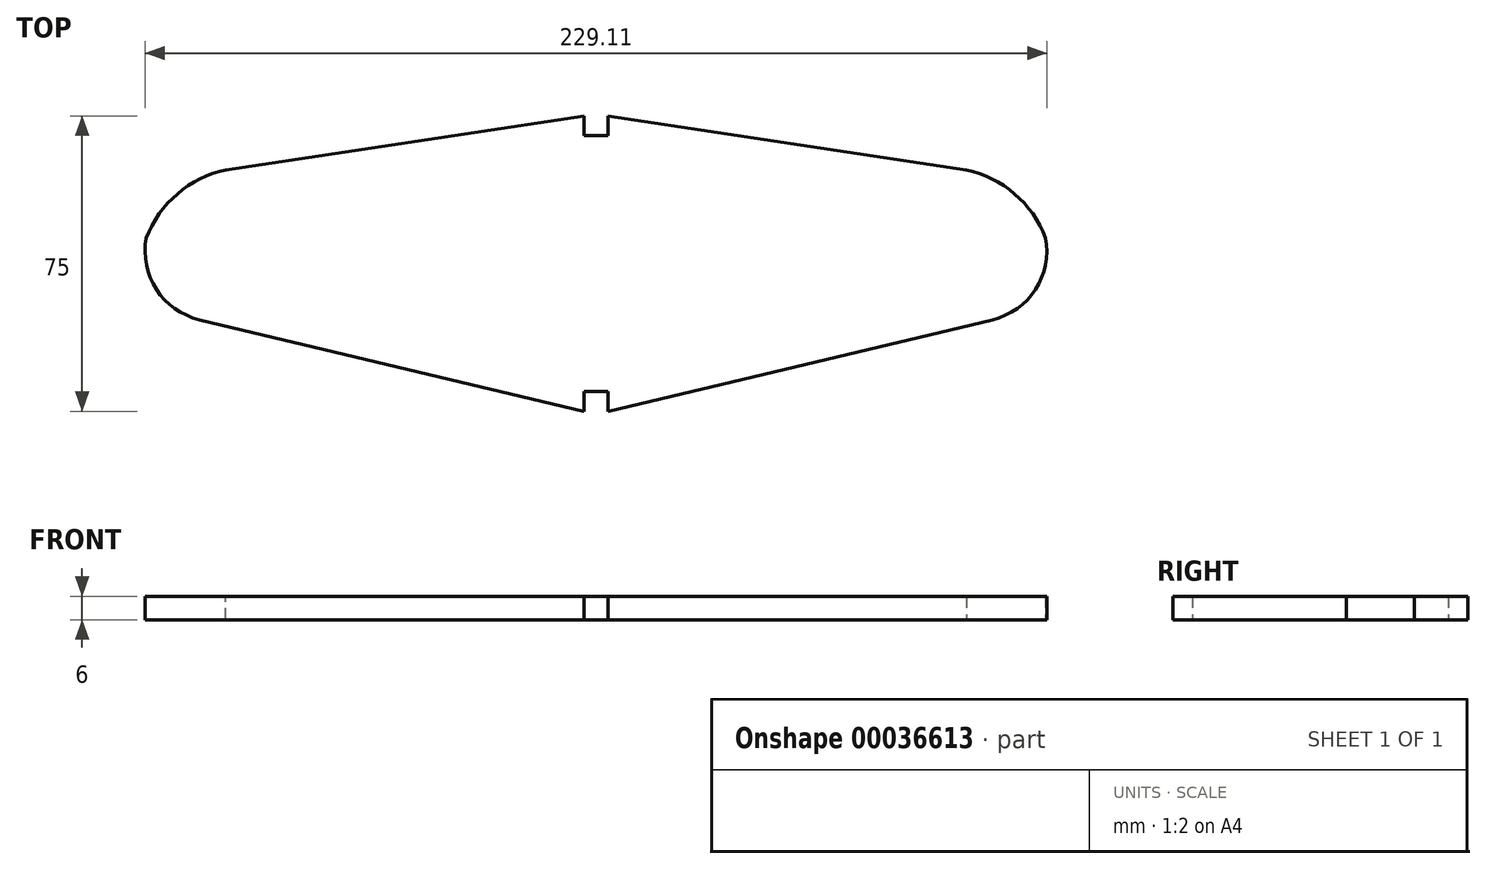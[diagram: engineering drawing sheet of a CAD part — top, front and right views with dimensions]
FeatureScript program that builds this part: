
annotation { "Feature Type Name" : "Feature", "Feature Type Description" : "" }
export const myFeature = defineFeature(function(context is Context, id is Id, definition is map)
    precondition{}
    {
        {
            var Q0;
            Q0=qCreatedBy(makeId("Top.planeOp"),FACE);
            var sketch = newSketch(context, id + "F0", { "sketchPlane" : qUnion([Q0])});
            skLineSegment(sketch, "E0", {"start": v(70, -8.54) * mm, "end": v(-27.72, -31.78) * mm});
            skLineSegment(sketch, "E1", {"start": v(-27.72, -31.78) * mm, "end": v(-27.72, 43.22) * mm});
            skLineSegment(sketch, "E2", {"start": v(-27.72, 43.22) * mm, "end": v(63.37, 29.54) * mm});
            skArc(sketch, "E3", {"start": v(83.53, 12.28) * mm, "mid": v(75.61, 23.44) * mm, "end": v(63.37, 29.54) * mm});
            skArc(sketch, "E4", {"start": v(70, -8.54) * mm, "mid": v(80.93, -0.84) * mm, "end": v(83.53, 12.28) * mm});
            skLineSegment(sketch, "E5", {"start": v(-27.72, 43.22) * mm, "end": v(-27.72, 38.22) * mm});
            skLineSegment(sketch, "E6", {"start": v(-27.72, -31.78) * mm, "end": v(-27.72, -26.78) * mm});
            skPoint(sketch, "E7.endSnap0", {"position": v(-27.72, 5.72) * mm});
            skLineSegment(sketch, "E8.bottom", {"start": v(-27.72, 38.22) * mm, "end": v(-30.72, 38.22) * mm});
            skLineSegment(sketch, "E8.top", {"start": v(-27.72, -26.78) * mm, "end": v(-30.72, -26.78) * mm});
            skLineSegment(sketch, "E8.left", {"start": v(-27.72, 38.22) * mm, "end": v(-27.72, -26.78) * mm});
            skLineSegment(sketch, "E8.right", {"start": v(-30.72, 38.22) * mm, "end": v(-30.72, -26.78) * mm});
            skSolve(sketch);
        }
        {
            var Q0;
            Q0=makeQuery(id+"F0.imprint","IMPRINT",FACE,{"disambiguationData":[TD([[makeQuery(id+"F0.imprint","IMPRINT",EDGE,{"derivedFrom":sQuery(id+"F0.wireOp",EDGE,"E0")}),-1.0]])]});
            var Q1;
            Q1=makeQuery(id+"F0.imprint","IMPRINT",FACE,{"disambiguationData":[TD([[makeQuery(id+"F0.imprint","IMPRINT",EDGE,{"derivedFrom":sQuery(id+"F0.wireOp",EDGE,"E2")}),-1.0]])]});
            var Q2;
            {var subQ3=sQuery(id+"F0.wireOp",EDGE,"E8.bottom");Q2=makeQuery(id+"F0.imprint","IMPRINT",FACE,{"disambiguationData":[TD([[makeQuery(id+"F0.imprint","IMPRINT",EDGE,{"derivedFrom":subQ3}),1.0]])]});}
            extrude(context, id + "F1", {"entities" : qUnion([Q0, Q1, Q2]), "depth" : 6 * mm});
        }
        {
            var Q0;
            Q0=makeQuery(id+"F1.opExtrude","SWEPT_FACE",FACE,{"disambiguationData":[OSD([sQuery(id+"F0.wireOp",EDGE,"E8.right")])]});
            var sketch = newSketch(context, id + "F2", { "sketchPlane" : qUnion([Q0])});
            skLineSegment(sketch, "E9", {"start": v(-38.22, 3) * mm, "end": v(26.78, 3) * mm});
            skSolve(sketch);
        }
        {
            var Q0;
            Q0=makeQuery(id+"F1.opExtrude","SWEPT_BODY",BODY,{"disambiguationData":[OSD([sQuery(id+"F0.wireOp",EDGE,"E0"),sQuery(id+"F0.wireOp",EDGE,"E2"),sQuery(id+"F0.wireOp",EDGE,"E3"),sQuery(id+"F0.wireOp",EDGE,"E4"),sQuery(id+"F0.wireOp",EDGE,"E5"),sQuery(id+"F0.wireOp",EDGE,"E6"),sQuery(id+"F0.wireOp",EDGE,"E8.bottom"),sQuery(id+"F0.wireOp",EDGE,"E8.top"),sQuery(id+"F0.wireOp",EDGE,"E8.right")])]});
            var Q1;
            Q1=sQuery(id+"F2.wireOp",EDGE,"E9");
            circularPattern(context, id + "F3", {"operationType" : NewBodyOperationType.ADD, "entities" : qUnion([Q0]), "axis" : qUnion([Q1]), "angle" : 180 * degree, "instanceCount" : 2});
        }
    });
